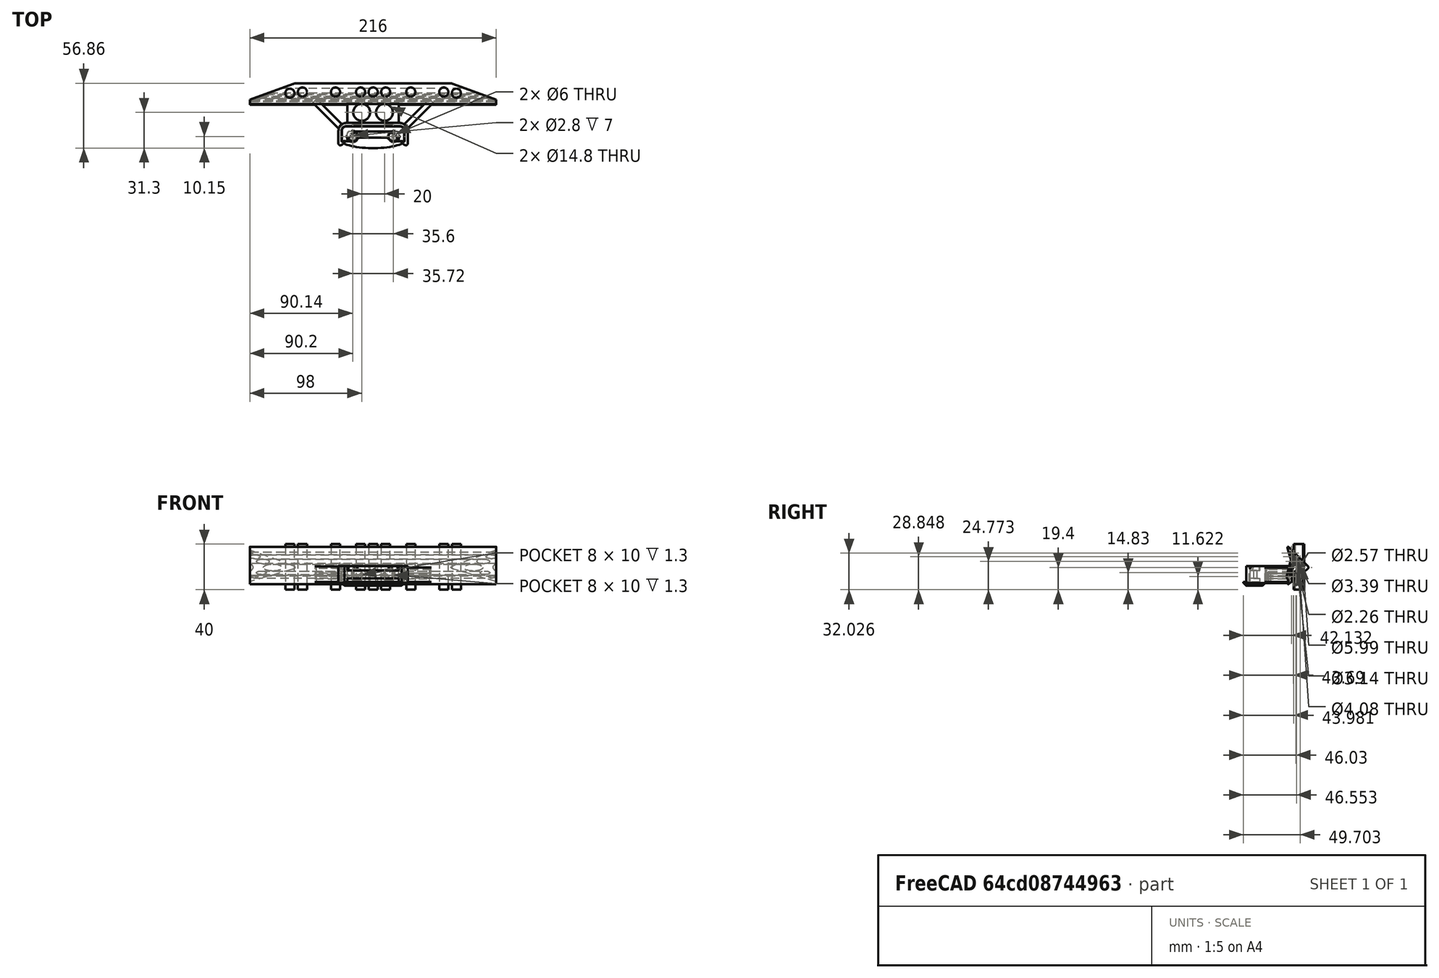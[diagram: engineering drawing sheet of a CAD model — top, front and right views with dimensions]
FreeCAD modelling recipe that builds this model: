
FCSTD DOCUMENT  (FreeCAD 0.21R0.20.1)
Label: 057
License: All rights reserved
LicenseURL: http://en.wikipedia.org/wiki/All_rights_reserved
objects: Part::Cylinder×29, Part::MultiFuse×13, Sketcher::SketchObject×7, Part::Extrusion×7, Part::Box×7, Part::Cut×6, Part::Fillet×5, Part::Chamfer×2
note: 76 computed .brp shape members not serialized (recipe doc carries the construction recipe); baked Part::Feature solids carry a one-line shape summary decoded from their .brp

FEATURE [Sketcher::SketchObject] Sketch  label="attatchmentPiece"
  FullyConstrained = true
  sketch-geometry (20):
    g0: LineSegment StartX=21.05 StartY=0 StartZ=0 EndX=21.05 EndY=-1 EndZ=0
    g1: LineSegment StartX=21.05 StartY=-1 StartZ=0 EndX=21.05 EndY=-4.3 EndZ=0
    g2: LineSegment StartX=-24.15 StartY=4.3 StartZ=0 EndX=21.05 EndY=4.3 EndZ=0
    g3: LineSegment StartX=21.05 StartY=0 StartZ=0 EndX=21.05 EndY=4.3 EndZ=0
    g4-g7: Circle x4 (B-spline internal-alignment scaffolding for g8; pole/knot coordinates omitted)
    g8: BSplineCurve PolesCount=4 KnotsCount=2 Degree=3 IsPeriodic=0
    g9: GeomPoint X=10.05 Y=-1 Z=0
    g10: GeomPoint X=14.55 Y=-4.3 Z=0
    g11: LineSegment StartX=10.05 StartY=-1 StartZ=0 EndX=-10.05 EndY=-1 EndZ=0
    g12: LineSegment StartX=14.55 StartY=-4.3 StartZ=0 EndX=21.05 EndY=-4.3 EndZ=0
    g13: LineSegment StartX=-24.15 StartY=4.3 StartZ=0 EndX=-24.15 EndY=-4.3 EndZ=0
    g14: LineSegment StartX=-13.15 StartY=-1 StartZ=0 EndX=-10.05 EndY=-1 EndZ=0
    g15: LineSegment StartX=-24.15 StartY=-4.3 StartZ=0 EndX=-19.35 EndY=-4.3 EndZ=0
    g16: LineSegment StartX=-19.35 StartY=-4.3 StartZ=0 EndX=-17.65 EndY=-4.3 EndZ=0
    g17: BSplineCurve PolesCount=4 KnotsCount=2 Degree=3 IsPeriodic=0
    g18: Circle CenterX=16.25 CenterY=0 CenterZ=0 NormalX=0 NormalY=0 NormalZ=1 AngleXU=0 Radius=1.4
    g19: Circle CenterX=-19.35 CenterY=0 CenterZ=0 NormalX=0 NormalY=0 NormalZ=1 AngleXU=0 Radius=1.4
  constraints (41):
    c: Vertical(g0)
    c: Coincident(g1,g0)
    c: Vertical(g1)
    c: Block(g0)
    c: Horizontal(g2)
    c: Vertical(g3)
    c: Coincident(g3,g2)
    c: Block(g2)
    c: Block(g3)
    c: Weight(g4) = 1
    c: Equal(g4,g5)
    c: Equal(g4,g6)
    c: Equal(g4,g7)
    c: InternalAlignment(g4-g7 -> g8) x4
    c: InternalAlignment(g9,g8)
    c: InternalAlignment(g10,g8)
    c: Block(g8)
    c: Coincident(g11,g8)
    c: Horizontal(g11)
    c: Coincident(g12,g8)
    c: Coincident(g12,g1)
    c: Horizontal(g12)
    c: Distance(g2) = 45.2
    c: Coincident(g13,g2)
    c: Vertical(g13)
    c: Horizontal(g14)
    c: Distance(g14) = 3.1
    c: Horizontal(g15)
    c: Block(g17)
    c: Coincident(g16,g15)
    c: Coincident(g16,g17)
    c: Horizontal(g16)
    c: Block(g16)
    c: Coincident(g17,g14)
    c: Block(g15)
    c: Block(g11)
    c: Block(g13)
    c: Distance(g15) = 4.8
    c: Distance(g16) = 1.7
    c: Block(g18)
    c: Block(g19)
FEATURE [Part::Extrusion] Extrude  label="attatchmentPiece001"
  Base = -> Sketch
  Dir = (0,0,1)
  DirMode = 2
  FaceMakerClass = Part::FaceMakerBullseye
  LengthFwd = 7
  LengthRev = 0
  Solid = true
  Symmetric = false
FEATURE [Sketcher::SketchObject] Sketch001  label="attatchmentPieceSurround"
  FullyConstrained = true
  sketch-geometry (18):
    g0: LineSegment StartX=25.85 StartY=-4.3 StartZ=0 EndX=21.05 EndY=-4.3 EndZ=0
    g1: LineSegment StartX=25.85 StartY=-4.3 StartZ=0 EndX=25.85 EndY=4.3 EndZ=0
    g2: LineSegment StartX=-21.05 StartY=8.9 StartZ=0 EndX=21.05 EndY=8.9 EndZ=0
    g3: Circle CenterX=21.05 CenterY=8.9 CenterZ=0 NormalX=0 NormalY=0 NormalZ=1 AngleXU=0 Radius=1
    g4: Circle CenterX=25.85 CenterY=8.9 CenterZ=0 NormalX=0 NormalY=0 NormalZ=1 AngleXU=0 Radius=1
    g5: Circle CenterX=25.85 CenterY=4.3 CenterZ=0 NormalX=0 NormalY=0 NormalZ=1 AngleXU=0 Radius=1
    g6: BSplineCurve PolesCount=3 KnotsCount=2 Degree=2 IsPeriodic=0
    g7: GeomPoint X=21.05 Y=8.9 Z=0
    g8: GeomPoint X=25.85 Y=4.3 Z=0
    g9: ArcOfCircle CenterX=19.45 CenterY=2.7 CenterZ=0 NormalX=0 NormalY=0 NormalZ=1 AngleXU=0 Radius=1.6 StartAngle=0 EndAngle=1.5708
    g10: LineSegment StartX=21.05 StartY=2.7 StartZ=0 EndX=21.05 EndY=-4.3 EndZ=0
    g11: BSplineCurve PolesCount=3 KnotsCount=2 Degree=2 IsPeriodic=0
    g12: LineSegment StartX=-28.95 StartY=-4.3 StartZ=0 EndX=-28.95 EndY=4.3 EndZ=0
    g13: LineSegment StartX=-24.15 StartY=-4.3 StartZ=0 EndX=-28.95 EndY=-4.3 EndZ=0
    g14: LineSegment StartX=-24.15 StartY=2.7 StartZ=0 EndX=-24.15 EndY=-4.3 EndZ=0
    g15: ArcOfCircle CenterX=-22.55 CenterY=2.7 CenterZ=0 NormalX=0 NormalY=0 NormalZ=1 AngleXU=0 Radius=1.6 StartAngle=1.5708 EndAngle=3.14159
    g16: LineSegment StartX=-24.15 StartY=8.9 StartZ=0 EndX=-21.05 EndY=8.9 EndZ=0
    g17: LineSegment StartX=-22.55 StartY=4.3 StartZ=0 EndX=19.45 EndY=4.3 EndZ=0
  constraints (38):
    c: Horizontal(g0)
    c: Vertical(g1)
    c: Coincident(g1,g0)
    c: Horizontal(g2)
    c: Distance(g2) = 42.1
    c: Block(g2)
    c: Coincident(g6,g2)
    c: Weight(g3) = 1
    c: Equal(g3,g4)
    c: Equal(g3,g5)
    c: Coincident(g6,g1)
    c: InternalAlignment(g3,g6)
    c: InternalAlignment(g4,g6)
    c: InternalAlignment(g5,g6)
    c: InternalAlignment(g7,g6)
    c: InternalAlignment(g8,g6)
    c: Block(g0)
    c: Block(g6)
    c: Block(g9)
    c: Coincident(g10,g9)
    c: Coincident(g10,g0)
    c: Vertical(g10)
    c: Horizontal(g13)
    c: Coincident(g12,g13)
    c: Vertical(g12)
    c: Coincident(g11,g12)
    c: Block(g12)
    c: Block(g11)
    c: Block(g15)
    c: Coincident(g14,g15)
    c: Coincident(g14,g13)
    c: Vertical(g14)
    c: Coincident(g16,g11)
    c: Coincident(g16,g2)
    c: Horizontal(g16)
    c: Coincident(g17,g15)
    c: Coincident(g17,g9)
    c: Horizontal(g17)
FEATURE [Part::Extrusion] Extrude001  label="attatchmentPieceSurround001"
  Base = -> Sketch001
  Dir = (0,0,1)
  DirMode = 2
  FaceMakerClass = Part::FaceMakerBullseye
  LengthFwd = 14.7
  LengthRev = 0
  Placement = pos=(0,0,-4.1) rot=(0,0,1;0rad)
  Solid = true
  Symmetric = false
FEATURE [Sketcher::SketchObject] Sketch002  label="attatchmentPieceEndScrewHoleCaps"
  FullyConstrained = true
  sketch-geometry (10):
    g0: ArcOfCircle CenterX=16.25 CenterY=0 CenterZ=0 NormalX=0 NormalY=0 NormalZ=1 AngleXU=0 Radius=4.3 StartAngle=2.05456 EndAngle=5.79942
    g1: LineSegment StartX=14.25 StartY=3.80657 StartZ=0 EndX=14.25 EndY=6 EndZ=0
    g2: LineSegment StartX=20.0566 StartY=-2 StartZ=0 EndX=22.25 EndY=-2 EndZ=0
    g3: LineSegment StartX=22.25 StartY=-2 StartZ=0 EndX=22.25 EndY=6 EndZ=0
    g4: LineSegment StartX=14.25 StartY=6 StartZ=0 EndX=22.25 EndY=6 EndZ=0
    g5: LineSegment StartX=-25.35 StartY=-2 StartZ=0 EndX=-25.35 EndY=6 EndZ=0
    g6: LineSegment StartX=-25.35 StartY=-2 StartZ=0 EndX=-23.1566 EndY=-2 EndZ=0
    g7: LineSegment StartX=-17.35 StartY=6 StartZ=0 EndX=-25.35 EndY=6 EndZ=0
    g8: LineSegment StartX=-17.35 StartY=3.80657 StartZ=0 EndX=-17.35 EndY=6 EndZ=0
    g9: ArcOfCircle CenterX=-19.35 CenterY=0 CenterZ=0 NormalX=0 NormalY=0 NormalZ=1 AngleXU=0 Radius=4.3 StartAngle=3.62536 EndAngle=7.37022
  constraints (25):
    c: Block(g0)
    c: Vertical(g1)
    c: Horizontal(g2)
    c: Coincident(g3,g2)
    c: Vertical(g3)
    c: Coincident(g4,g1)
    c: Horizontal(g4)
    c: Coincident(g3,g4)
    c: Block(g4)
    c: Block(g3)
    c: Coincident(g0,g1)
    c: Coincident(g0,g2)
    c: Block(g1)
    c: Block(g9)
    c: Horizontal(g6)
    c: Vertical(g8)
    c: Coincident(g7,g8)
    c: Horizontal(g7)
    c: Coincident(g5,g6)
    c: Vertical(g5)
    c: Coincident(g5,g7)
    c: Block(g7)
    c: Block(g5)
    c: Coincident(g9,g6)
    c: Coincident(g9,g8)
FEATURE [Part::Extrusion] Extrude002  label="attatchmentPieceEndScrewHoleCaps001"
  Base = -> Sketch002
  Dir = (0,0,1)
  DirMode = 2
  FaceMakerClass = Part::FaceMakerBullseye
  LengthFwd = 3.6
  LengthRev = 0
  Placement = pos=(0,0,7) rot=(0,0,1;0rad)
  Solid = true
  Symmetric = false
FEATURE [Sketcher::SketchObject] Sketch003  label="mainBumpperPieceAttatchment"
  FullyConstrained = true
  sketch-geometry (42):
    g0: Circle CenterX=28.85 CenterY=4.3 CenterZ=0 NormalX=0 NormalY=0 NormalZ=1 AngleXU=0 Radius=1
    g1: Circle CenterX=28.85 CenterY=11.9 CenterZ=0 NormalX=0 NormalY=0 NormalZ=1 AngleXU=0 Radius=1
    g2: Circle CenterX=21.05 CenterY=11.9 CenterZ=0 NormalX=0 NormalY=0 NormalZ=1 AngleXU=0 Radius=1
    g3: BSplineCurve PolesCount=3 KnotsCount=2 Degree=2 IsPeriodic=0
    g4: GeomPoint X=28.85 Y=4.3 Z=0
    g5: GeomPoint X=21.05 Y=11.9 Z=0
    g6: LineSegment StartX=-21.05 StartY=11.9 StartZ=0 EndX=21.05 EndY=11.9 EndZ=0
    g7: LineSegment StartX=28.85 StartY=4.3 StartZ=0 EndX=28.85 EndY=-4.3 EndZ=0
    g8: Circle CenterX=21.05 CenterY=9.2 CenterZ=0 NormalX=0 NormalY=0 NormalZ=1 AngleXU=0 Radius=1
    g9: Circle CenterX=26.15 CenterY=9.2 CenterZ=0 NormalX=0 NormalY=0 NormalZ=1 AngleXU=0 Radius=1
    g10: Circle CenterX=26.15 CenterY=4.3 CenterZ=0 NormalX=0 NormalY=0 NormalZ=1 AngleXU=0 Radius=1
    g11: BSplineCurve PolesCount=3 KnotsCount=2 Degree=2 IsPeriodic=0
    g12: GeomPoint X=21.05 Y=9.2 Z=0
    g13: GeomPoint X=26.15 Y=4.3 Z=0
    g14: LineSegment StartX=-21.05 StartY=9.2 StartZ=0 EndX=21.05 EndY=9.2 EndZ=0
    g15: LineSegment StartX=26.15 StartY=-4.3 StartZ=0 EndX=26.15 EndY=4.3 EndZ=0
    g16: LineSegment StartX=26.15 StartY=-4.3 StartZ=0 EndX=26.15 EndY=-4.6 EndZ=0
    g17: LineSegment StartX=23.45 StartY=-4.6 StartZ=0 EndX=26.15 EndY=-4.6 EndZ=0
    g18: LineSegment StartX=28.85 StartY=-4.3 StartZ=0 EndX=28.85 EndY=-7.9 EndZ=0
    g19: LineSegment StartX=23.45 StartY=-4.6 StartZ=0 EndX=23.45 EndY=-5.3 EndZ=0
    g20: Circle CenterX=28.85 CenterY=-7.9 CenterZ=0 NormalX=0 NormalY=0 NormalZ=1 AngleXU=0 Radius=1
    g21: Circle CenterX=26.15 CenterY=-8.2 CenterZ=0 NormalX=0 NormalY=0 NormalZ=1 AngleXU=0 Radius=1
    g22: Circle CenterX=23.45 CenterY=-5.3 CenterZ=0 NormalX=0 NormalY=0 NormalZ=1 AngleXU=0 Radius=1
    g23: BSplineCurve PolesCount=3 KnotsCount=2 Degree=2 IsPeriodic=0
    g24: GeomPoint X=28.85 Y=-7.9 Z=0
    g25: GeomPoint X=23.45 Y=-5.3 Z=0
    g26: LineSegment StartX=-21.05 StartY=9.2 StartZ=0 EndX=-24.15 EndY=9.2 EndZ=0
    g27: BSplineCurve PolesCount=3 KnotsCount=2 Degree=2 IsPeriodic=0
    g28: LineSegment StartX=-29.25 StartY=-4.3 StartZ=0 EndX=-29.25 EndY=-4.6 EndZ=0
    g29: LineSegment StartX=-29.25 StartY=-4.6 StartZ=0 EndX=-26.55 EndY=-4.6 EndZ=0
    g30: LineSegment StartX=-31.95 StartY=-4.3 StartZ=0 EndX=-31.95 EndY=-7.9 EndZ=0
    g31: LineSegment StartX=-26.55 StartY=-4.6 StartZ=0 EndX=-26.55 EndY=-5.3 EndZ=0
    g32: Circle CenterX=-31.95 CenterY=-7.9 CenterZ=0 NormalX=0 NormalY=0 NormalZ=1 AngleXU=0 Radius=1
    g33: Circle CenterX=-29.25 CenterY=-8.2 CenterZ=0 NormalX=0 NormalY=0 NormalZ=1 AngleXU=0 Radius=1
    g34: Circle CenterX=-26.55 CenterY=-5.3 CenterZ=0 NormalX=0 NormalY=0 NormalZ=1 AngleXU=0 Radius=1
    g35: BSplineCurve PolesCount=3 KnotsCount=2 Degree=2 IsPeriodic=0
    g36: GeomPoint X=-31.95 Y=-7.9 Z=0
    g37: GeomPoint X=-26.55 Y=-5.3 Z=0
    g38: LineSegment StartX=-31.95 StartY=4.3 StartZ=0 EndX=-31.95 EndY=-4.3 EndZ=0
    g39: LineSegment StartX=-29.25 StartY=-4.3 StartZ=0 EndX=-29.25 EndY=4.3 EndZ=0
    g40: BSplineCurve PolesCount=3 KnotsCount=2 Degree=2 IsPeriodic=0
    g41: LineSegment StartX=-21.05 StartY=11.9 StartZ=0 EndX=-24.15 EndY=11.9 EndZ=0
  constraints (78):
    c: Weight(g0) = 1
    c: Equal(g0,g1)
    c: Equal(g0,g2)
    c: InternalAlignment(g0,g3)
    c: InternalAlignment(g1,g3)
    c: InternalAlignment(g2,g3)
    c: InternalAlignment(g4,g3)
    c: InternalAlignment(g5,g3)
    c: Block(g3)
    c: Horizontal(g6)
    c: Vertical(g7)
    c: Block(g7)
    c: Block(g6)
    c: Weight(g8) = 1
    c: Equal(g8,g9)
    c: Equal(g8,g10)
    c: InternalAlignment(g8,g11)
    c: InternalAlignment(g9,g11)
    c: InternalAlignment(g10,g11)
    c: InternalAlignment(g12,g11)
    c: InternalAlignment(g13,g11)
    c: Horizontal(g14)
    c: Vertical(g15)
    c: Block(g11)
    c: Block(g15)
    c: Block(g14)
    c: Coincident(g16,g15)
    c: Vertical(g16)
    c: Distance(g16) = 0.3
    c: Horizontal(g17)
    c: Coincident(g17,g16)
    c: Coincident(g18,g7)
    c: Vertical(g18)
    c: Distance(g18) = 3.6
    c: Vertical(g19)
    c: Coincident(g19,g17)
    c: Coincident(g23,g18)
    c: Weight(g20) = 1
    c: Equal(g20,g21)
    c: Equal(g20,g22)
    c: Coincident(g23,g19)
    c: InternalAlignment(g20,g23)
    c: InternalAlignment(g21,g23)
    c: InternalAlignment(g22,g23)
    c: InternalAlignment(g24,g23)
    c: InternalAlignment(g25,g23)
    c: Block(g23)
    c: Horizontal(g26)
    c: Distance(g26) = 3.1
    c: Block(g27)
    c: Vertical(g38)
    c: Block(g38)
    c: Vertical(g39)
    c: Block(g40)
    c: Block(g39)
    c: Vertical(g28)
    c: Coincident(g28,g39)
    c: Coincident(g29,g28)
    c: Horizontal(g29)
    c: Vertical(g30)
    c: Coincident(g30,g38)
    c: Coincident(g31,g29)
    c: Vertical(g31)
    c: Coincident(g35,g30)
    c: Equal(g32,g33)
    c: Equal(g32,g34)
    c: Coincident(g35,g31)
    c: InternalAlignment(g32,g35)
    c: InternalAlignment(g33,g35)
    c: InternalAlignment(g34,g35)
    c: InternalAlignment(g36,g35)
    c: InternalAlignment(g37,g35)
    c: Block(g35)
    c: Coincident(g40,g26)
    c: Block(g29)
    c: Horizontal(g41)
    c: Equal(g26,g41) = 3.1
    c: Coincident(g41,g6)
FEATURE [Part::Box] Box  label="bumpperExtension"
  AttacherType = Attacher::AttachEngine3D
  Height = 14.7
  Length = 45.2
  Placement = pos=(-24.15,11.9,-4.1) rot=(0,0,1;0rad)
  Width = 18
FEATURE [Sketcher::SketchObject] Sketch004  label="bumpperMain"
  FullyConstrained = true
  Placement = pos=(0,0,0) rot=(0.57735,0.57735,0.57735;2.0944rad)
  sketch-geometry (62):
    g0: Circle CenterX=-3.12329 CenterY=2.49901 CenterZ=0 NormalX=0 NormalY=0 NormalZ=1 AngleXU=0 Radius=1
    g1: Circle CenterX=0 CenterY=0 CenterZ=0 NormalX=0 NormalY=0 NormalZ=1 AngleXU=0 Radius=1
    g2: Circle CenterX=-1.35243 CenterY=3.60648 CenterZ=0 NormalX=0 NormalY=0 NormalZ=1 AngleXU=0 Radius=1
    g3: BSplineCurve PolesCount=3 KnotsCount=2 Degree=2 IsPeriodic=0
    g4: GeomPoint X=-3.12329 Y=2.49901 Z=0
    g5: GeomPoint X=-1.35243 Y=3.60648 Z=0
    g6: Circle CenterX=-2.83953 CenterY=33.0261 CenterZ=0 NormalX=0 NormalY=0 NormalZ=1 AngleXU=0 Radius=1
    g7: Circle CenterX=0 CenterY=35.8434 CenterZ=0 NormalX=0 NormalY=0 NormalZ=1 AngleXU=0 Radius=1
    g8: Circle CenterX=-1.15771 CenterY=32.0146 CenterZ=0 NormalX=0 NormalY=0 NormalZ=1 AngleXU=0 Radius=1
    g9: BSplineCurve PolesCount=3 KnotsCount=2 Degree=2 IsPeriodic=0
    g10: GeomPoint X=-2.83953 Y=33.0261 Z=0
    g11: GeomPoint X=-1.15771 Y=32.0146 Z=0
    g12: Circle CenterX=-18.2963 CenterY=17.6904 CenterZ=0 NormalX=0 NormalY=0 NormalZ=1 AngleXU=0 Radius=1
    g13: Circle CenterX=-20 CenterY=16 CenterZ=0 NormalX=0 NormalY=0 NormalZ=1 AngleXU=0 Radius=1
    g14: Circle CenterX=-18.1259 CenterY=14.5008 CenterZ=0 NormalX=0 NormalY=0 NormalZ=1 AngleXU=0 Radius=1
    g15: BSplineCurve PolesCount=3 KnotsCount=2 Degree=2 IsPeriodic=0
    g16: GeomPoint X=-18.2963 Y=17.6904 Z=0
    g17: GeomPoint X=-18.1259 Y=14.5008 Z=0
    g18: LineSegment StartX=-18.2963 StartY=17.6904 StartZ=0 EndX=-2.83953 EndY=33.0261 EndZ=0
    g19: LineSegment StartX=-18.1259 StartY=14.5008 StartZ=0 EndX=-3.12329 EndY=2.49901 EndZ=0
    g20: Circle CenterX=-11.9527 CenterY=16 CenterZ=0 NormalX=0 NormalY=0 NormalZ=1 AngleXU=0 Radius=2.99582
    g21: Circle CenterX=-8.803 CenterY=21.3731 CenterZ=0 NormalX=0 NormalY=0 NormalZ=1 AngleXU=0 Radius=2.03939
    g22: Circle CenterX=-6.23123 CenterY=25.4475 CenterZ=0 NormalX=0 NormalY=0 NormalZ=1 AngleXU=0 Radius=1.69309
    g23: Circle CenterX=-4.38186 CenterY=28.6261 CenterZ=0 NormalX=0 NormalY=0 NormalZ=1 AngleXU=0 Radius=1.13029
    g24: Circle CenterX=-8.28033 CenterY=11.4296 CenterZ=0 NormalX=0 NormalY=0 NormalZ=1 AngleXU=0 Radius=1.57213
    g25: Circle CenterX=-5.93972 CenterY=8.22213 CenterZ=0 NormalX=0 NormalY=0 NormalZ=1 AngleXU=0 Radius=1.28743
    g26: Circle CenterX=-3.47023 CenterY=24.3665 CenterZ=0 NormalX=0 NormalY=0 NormalZ=1 AngleXU=0 Radius=1
    g27: Circle CenterX=-3.90437 CenterY=22.9307 CenterZ=0 NormalX=0 NormalY=0 NormalZ=1 AngleXU=0 Radius=1
    g28: Circle CenterX=-3.53772 CenterY=21.4762 CenterZ=0 NormalX=0 NormalY=0 NormalZ=1 AngleXU=0 Radius=1
    g29: BSplineCurve PolesCount=3 KnotsCount=2 Degree=2 IsPeriodic=0
    g30: GeomPoint X=-3.47023 Y=24.3665 Z=0
    g31: GeomPoint X=-3.53772 Y=21.4762 Z=0
    g32: LineSegment StartX=-1.15771 StartY=32.0146 StartZ=0 EndX=-3.47023 EndY=24.3665 EndZ=0
    g33: Circle CenterX=-5.41867 CenterY=17.9226 CenterZ=0 NormalX=0 NormalY=0 NormalZ=1 AngleXU=0 Radius=1
    g34: Circle CenterX=-6 CenterY=16 CenterZ=0 NormalX=0 NormalY=0 NormalZ=1 AngleXU=0 Radius=1
    g35: Circle CenterX=-5.22753 CenterY=13.9401 CenterZ=0 NormalX=0 NormalY=0 NormalZ=1 AngleXU=0 Radius=1
    g36: BSplineCurve PolesCount=3 KnotsCount=2 Degree=2 IsPeriodic=0
    g37: GeomPoint X=-5.41867 Y=17.9226 Z=0
    g38: GeomPoint X=-5.22753 Y=13.9401 Z=0
    g39: Circle CenterX=-3.98946 CenterY=10.6386 CenterZ=0 NormalX=0 NormalY=0 NormalZ=1 AngleXU=0 Radius=1
    g40: Circle CenterX=-2.58497 CenterY=6.89324 CenterZ=0 NormalX=0 NormalY=0 NormalZ=1 AngleXU=0 Radius=1
    g41: Circle CenterX=-3.11001 CenterY=10.8586 CenterZ=0 NormalX=0 NormalY=0 NormalZ=1 AngleXU=0 Radius=1
    g42: BSplineCurve PolesCount=3 KnotsCount=2 Degree=2 IsPeriodic=0
    g43: GeomPoint X=-3.98946 Y=10.6386 Z=0
    g44: GeomPoint X=-3.11001 Y=10.8586 Z=0
    g45: Circle CenterX=-1.35243 CenterY=3.60648 CenterZ=0 NormalX=0 NormalY=0 NormalZ=1 AngleXU=0 Radius=1
    g46: Circle CenterX=-1.76142 CenterY=4.69712 CenterZ=0 NormalX=0 NormalY=0 NormalZ=1 AngleXU=0 Radius=1
    g47: Circle CenterX=-1.05937 CenterY=5.79125 CenterZ=0 NormalX=0 NormalY=0 NormalZ=1 AngleXU=0 Radius=1
    g48: BSplineCurve PolesCount=3 KnotsCount=2 Degree=2 IsPeriodic=0
    g49: GeomPoint X=-1.35243 Y=3.60648 Z=0
    g50: GeomPoint X=-1.05937 Y=5.79125 Z=0
    g51: Circle CenterX=-0.519336 CenterY=6.6329 CenterZ=0 NormalX=0 NormalY=0 NormalZ=1 AngleXU=0 Radius=1
    g52: Circle CenterX=0 CenterY=7.44228 CenterZ=0 NormalX=0 NormalY=0 NormalZ=1 AngleXU=0 Radius=1
    g53: Circle CenterX=-0.244436 CenterY=8.41194 CenterZ=0 NormalX=0 NormalY=0 NormalZ=1 AngleXU=0 Radius=1
    g54: BSplineCurve PolesCount=3 KnotsCount=2 Degree=2 IsPeriodic=0
    g55: GeomPoint X=-0.519336 Y=6.6329 Z=0
    g56: GeomPoint X=-0.244436 Y=8.41194 Z=0
    g57: LineSegment StartX=-3.53772 StartY=21.4762 StartZ=0 EndX=-0.244436 EndY=8.41194 EndZ=0
    g58: LineSegment StartX=-5.22753 StartY=13.9401 StartZ=0 EndX=-3.98946 EndY=10.6386 EndZ=0
    g59: LineSegment StartX=-1.05937 StartY=5.79125 StartZ=0 EndX=-0.519336 EndY=6.6329 EndZ=0
    g60: BSplineCurve PolesCount=3 KnotsCount=2 Degree=2 IsPeriodic=0
    g61: LineSegment StartX=-4.0304 StartY=17.8099 StartZ=0 EndX=-3.11001 EndY=10.8586 EndZ=0
  constraints (96):
    c: Weight(g0) = 1
    c: Equal(g0,g1)
    c: Equal(g0,g2)
    c: InternalAlignment(g0,g3)
    c: InternalAlignment(g1,g3)
    c: InternalAlignment(g2,g3)
    c: InternalAlignment(g4,g3)
    c: InternalAlignment(g5,g3)
    c: Block(g3)
    c: Weight(g6) = 1
    c: Equal(g6,g7)
    c: Equal(g6,g8)
    c: InternalAlignment(g6,g9)
    c: InternalAlignment(g7,g9)
    c: InternalAlignment(g8,g9)
    c: InternalAlignment(g10,g9)
    c: InternalAlignment(g11,g9)
    c: Block(g9)
    c: Weight(g12) = 1
    c: Equal(g12,g13)
    c: Equal(g12,g14)
    c: InternalAlignment(g12,g15)
    c: InternalAlignment(g13,g15)
    c: InternalAlignment(g14,g15)
    c: InternalAlignment(g16,g15)
    c: InternalAlignment(g17,g15)
    c: Block(g15)
    c: Coincident(g18,g15)
    c: Coincident(g18,g9)
    c: Coincident(g19,g15)
    c: Coincident(g19,g3)
    c: Block(g25)
    c: Block(g24)
    c: Block(g20)
    c: Block(g21)
    c: Block(g22)
    c: Block(g23)
    c: Weight(g26) = 1
    c: Equal(g26,g27)
    c: Equal(g26,g28)
    c: InternalAlignment(g26,g29)
    c: InternalAlignment(g27,g29)
    c: InternalAlignment(g28,g29)
    c: InternalAlignment(g30,g29)
    c: InternalAlignment(g31,g29)
    c: Block(g29)
    c: Coincident(g32,g9)
    c: Coincident(g32,g29)
    c: Weight(g33) = 1
    c: Equal(g33,g34)
    c: Equal(g33,g35)
    c: InternalAlignment(g33,g36)
    c: InternalAlignment(g34,g36)
    c: InternalAlignment(g35,g36)
    c: InternalAlignment(g37,g36)
    c: InternalAlignment(g38,g36)
    c: Block(g36)
    c: Weight(g39) = 1
    c: Equal(g39,g40)
    c: Equal(g39,g41)
    c: InternalAlignment(g39,g42)
    c: InternalAlignment(g40,g42)
    c: InternalAlignment(g41,g42)
    c: InternalAlignment(g43,g42)
    c: InternalAlignment(g44,g42)
    c: Block(g42)
    c: Coincident(g48,g3)
    c: Weight(g45) = 1
    c: Equal(g45,g46)
    c: Equal(g45,g47)
    c: InternalAlignment(g45,g48)
    c: InternalAlignment(g46,g48)
    c: InternalAlignment(g47,g48)
    c: InternalAlignment(g49,g48)
    c: InternalAlignment(g50,g48)
    c: Block(g48)
    c: Weight(g51) = 1
    c: Equal(g51,g52)
    c: Equal(g51,g53)
    c: InternalAlignment(g51,g54)
    c: InternalAlignment(g52,g54)
    c: InternalAlignment(g53,g54)
    c: InternalAlignment(g55,g54)
    c: InternalAlignment(g56,g54)
    c: Block(g54)
    c: Coincident(g57,g29)
    c: Coincident(g57,g54)
    c: Block(g57)
    c: Coincident(g58,g36)
    c: Coincident(g58,g42)
    c: Coincident(g59,g48)
    c: Coincident(g59,g54)
    c: Block(g60)
    c: Coincident(g60,g36)
    c: Coincident(g61,g60)
    c: Coincident(g61,g42)
FEATURE [Part::Extrusion] Extrude004  label="bumpperMain001"
  Base = -> Sketch004
  Dir = (1,0,0)
  DirMode = 2
  FaceMakerClass = Part::FaceMakerBullseye
  LengthFwd = 216
  LengthRev = 0
  Placement = pos=(106.45,27.6,-6.6) rot=(0,0,1;3.14159rad)
  Solid = true
  Symmetric = false
FEATURE [Sketcher::SketchObject] Sketch005  label="attatchmentPieceBottom"
  FullyConstrained = true
  sketch-geometry (20):
    g0: LineSegment StartX=25.85 StartY=-4.3 StartZ=0 EndX=25.85 EndY=4.3 EndZ=0
    g1: LineSegment StartX=-21.05 StartY=8.9 StartZ=0 EndX=21.05 EndY=8.9 EndZ=0
    g2: Circle CenterX=21.05 CenterY=8.9 CenterZ=0 NormalX=0 NormalY=0 NormalZ=1 AngleXU=0 Radius=1
    g3: Circle CenterX=25.85 CenterY=8.9 CenterZ=0 NormalX=0 NormalY=0 NormalZ=1 AngleXU=0 Radius=1
    g4: Circle CenterX=25.85 CenterY=4.3 CenterZ=0 NormalX=0 NormalY=0 NormalZ=1 AngleXU=0 Radius=1
    g5: BSplineCurve PolesCount=3 KnotsCount=2 Degree=2 IsPeriodic=0
    g6: GeomPoint X=21.05 Y=8.9 Z=0
    g7: GeomPoint X=25.85 Y=4.3 Z=0
    g8: BSplineCurve PolesCount=3 KnotsCount=2 Degree=2 IsPeriodic=0
    g9: LineSegment StartX=-28.95 StartY=-4.3 StartZ=0 EndX=-28.95 EndY=4.3 EndZ=0
    g10: LineSegment StartX=-24.15 StartY=8.9 StartZ=0 EndX=-21.05 EndY=8.9 EndZ=0
    g11: Circle CenterX=-19.41 CenterY=0 CenterZ=0 NormalX=0 NormalY=0 NormalZ=1 AngleXU=0 Radius=3
    g12: Circle CenterX=16.3103 CenterY=0 CenterZ=0 NormalX=0 NormalY=0 NormalZ=1 AngleXU=0 Radius=3
    g13-g16: Circle x4 (B-spline internal-alignment scaffolding for g17; pole/knot coordinates omitted)
    g17: BSplineCurve PolesCount=4 KnotsCount=2 Degree=3 IsPeriodic=0
    g18: GeomPoint X=-28.95 Y=-4.3 Z=0
    g19: GeomPoint X=25.85 Y=-4.3 Z=0
  constraints (36):
    c: Vertical(g0)
    c: Horizontal(g1)
    c: Distance(g1) = 42.1
    c: Block(g1)
    c: Coincident(g5,g1)
    c: Weight(g2) = 1
    c: Equal(g2,g3)
    c: Equal(g2,g4)
    c: Coincident(g5,g0)
    c: InternalAlignment(g2,g5)
    c: InternalAlignment(g3,g5)
    c: InternalAlignment(g4,g5)
    c: InternalAlignment(g6,g5)
    c: InternalAlignment(g7,g5)
    c: Block(g5)
    c: Vertical(g9)
    c: Coincident(g8,g9)
    c: Block(g9)
    c: Block(g8)
    c: Coincident(g10,g8)
    c: Coincident(g10,g1)
    c: Horizontal(g10)
    c: PointOnObject(g12,g-1)
    c: PointOnObject(g11,g-1)
    c: Block(g11)
    c: Block(g12)
    c: Coincident(g17,g9)
    c: Weight(g13) = 1
    c: Equal(g13,g14)
    c: Equal(g13,g15)
    c: Equal(g13,g16)
    c: Coincident(g17,g0)
    c: InternalAlignment(g13-g16 -> g17) x4
    c: InternalAlignment(g18,g17)
    c: InternalAlignment(g19,g17)
    c: Block(g17)
FEATURE [Part::Extrusion] Extrude005  label="removeFromMainBumpperPieceAttatchment"
  Base = -> Sketch005
  Dir = (0,0,1)
  DirMode = 2
  FaceMakerClass = Part::FaceMakerBullseye
  LengthFwd = 3.2
  LengthRev = 0
  Placement = pos=(0,0,-6.2) rot=(0,0,1;0rad)
  Solid = true
  Symmetric = false
FEATURE [Part::Extrusion] Extrude006  label="mainBumpperPieceAttatchment001"
  Base = -> Sketch003
  Dir = (0,0,1)
  DirMode = 2
  FaceMakerClass = Part::FaceMakerBullseye
  LengthFwd = 14.7
  LengthRev = 0
  Placement = pos=(0,0,-4.1) rot=(0,0,1;0rad)
  Solid = true
  Symmetric = false
FEATURE [Part::Cylinder] Cylinder  label="removeFromBumpperExtension"
  Angle = 360
  AttacherType = Attacher::AttachEngine3D
  FirstAngle = 0
  Height = 20
  Placement = pos=(8.45,21.15,-8) rot=(0,0,1;0rad)
  Radius = 7.4
  SecondAngle = 0
FEATURE [Part::Cylinder] Cylinder001  label="removeFromBumpperExtension001"
  Angle = 360
  AttacherType = Attacher::AttachEngine3D
  FirstAngle = 0
  Height = 20
  Placement = pos=(-11.55,21.15,-8) rot=(0,0,1;0rad)
  Radius = 7.4
  SecondAngle = 0
FEATURE [Part::MultiFuse] Fusion  label="removeFromBumpperExtension002"
  Shapes = -> [Cylinder,Cylinder001]
FEATURE [Part::Cylinder] Cylinder002  label="removeFromBumpperExtension004"
  Angle = 360
  AttacherType = Attacher::AttachEngine3D
  FirstAngle = 0
  Height = 20
  Placement = pos=(8.45,21.15,-8) rot=(0,0,1;0rad)
  Radius = 7.4
  SecondAngle = 0
FEATURE [Part::Cylinder] Cylinder003  label="removeFromBumpperExtension005"
  Angle = 360
  AttacherType = Attacher::AttachEngine3D
  FirstAngle = 0
  Height = 20
  Placement = pos=(-11.55,21.15,-8) rot=(0,0,1;0rad)
  Radius = 7.4
  SecondAngle = 0
FEATURE [Part::MultiFuse] Fusion001  label="removeFromBumpperMain"
  Shapes = -> [Cylinder002,Cylinder003]
FEATURE [Part::Cut] Cut  label="bumpperExtension001"
  Base = -> Box
  Tool = -> Fusion
FEATURE [Part::Fillet] Fillet  label="bumpperExtension002"
  Base = -> Cut
  Edges = 4 edges r=3: [Edge2,Edge4,Edge9,Edge14]
FEATURE [Part::Box] Box001  label="bumpperExtensionBumpHole"
  AttacherType = Attacher::AttachEngine3D
  Height = 10
  Length = 8
  Placement = pos=(8.45,9.2,-1.8) rot=(0,0,1;0rad)
  Width = 1.3
FEATURE [Part::Box] Box002  label="bumpperExtensionBumpHole001"
  AttacherType = Attacher::AttachEngine3D
  Height = 10
  Length = 8
  Placement = pos=(-19.55,9.2,-1.8) rot=(0,0,1;0rad)
  Width = 1.3
FEATURE [Part::Box] Box003  label="attatchmentPieceSurroundBump"
  AttacherType = Attacher::AttachEngine3D
  Height = 9.2
  Length = 7.2
  Placement = pos=(8.85,8.9,-1.4) rot=(0,0,1;0rad)
  Width = 1.3
FEATURE [Part::Box] Box004  label="attatchmentPieceSurroundBump001"
  AttacherType = Attacher::AttachEngine3D
  Height = 9.2
  Length = 7.2
  Placement = pos=(-19.15,8.9,-1.4) rot=(0,0,1;0rad)
  Width = 1.3
FEATURE [Part::MultiFuse] Fusion002  label="attatchmentPieceSurroundBump002"
  Placement = pos=(0,-0.4,0) rot=(0,0,1;0rad)
  Shapes = -> [Box004,Box003]
FEATURE [Part::MultiFuse] Fusion003  label="bumpperExtensionBumpHole002"
  Shapes = -> [Box002,Box001]
FEATURE [Part::Cut] Cut002  label="mainBumpperPieceAttatchment002"
  Base = -> Extrude006
  Tool = -> Fusion003
FEATURE [Part::Fillet] Fillet003  label="attatchmentPieceEndScrewHoleCaps002"
  Base = -> Extrude002
  Edges = 6 edges r=2.4: [Edge4,Edge7,Edge15,Edge25,Edge28,Edge30]
FEATURE [Part::Fillet] Fillet004  label="attatchmentPieceSurround002"
  Base = -> Extrude001
  Edges = 3 edges r=1.2: [Edge19,Edge25,Edge31]
FEATURE [Part::Fillet] Fillet006  label="mainBumpperPieceAttatchment003"
  Base = -> Cut002
  Edges = 2 edges r=1.6: [Edge2,Edge55]
FEATURE [Sketcher::SketchObject] Sketch006  label="attatchmentPieceBottom002"
  FullyConstrained = true
  sketch-geometry (20):
    g0: LineSegment StartX=25.85 StartY=-4.3 StartZ=0 EndX=25.85 EndY=4.3 EndZ=0
    g1: LineSegment StartX=-21.05 StartY=8.9 StartZ=0 EndX=21.05 EndY=8.9 EndZ=0
    g2: Circle CenterX=21.05 CenterY=8.9 CenterZ=0 NormalX=0 NormalY=0 NormalZ=1 AngleXU=0 Radius=1
    g3: Circle CenterX=25.85 CenterY=8.9 CenterZ=0 NormalX=0 NormalY=0 NormalZ=1 AngleXU=0 Radius=1
    g4: Circle CenterX=25.85 CenterY=4.3 CenterZ=0 NormalX=0 NormalY=0 NormalZ=1 AngleXU=0 Radius=1
    g5: BSplineCurve PolesCount=3 KnotsCount=2 Degree=2 IsPeriodic=0
    g6: GeomPoint X=21.05 Y=8.9 Z=0
    g7: GeomPoint X=25.85 Y=4.3 Z=0
    g8: BSplineCurve PolesCount=3 KnotsCount=2 Degree=2 IsPeriodic=0
    g9: LineSegment StartX=-28.95 StartY=-4.3 StartZ=0 EndX=-28.95 EndY=4.3 EndZ=0
    g10: LineSegment StartX=-24.15 StartY=8.9 StartZ=0 EndX=-21.05 EndY=8.9 EndZ=0
    g11: Circle CenterX=-19.41 CenterY=0 CenterZ=0 NormalX=0 NormalY=0 NormalZ=1 AngleXU=0 Radius=3
    g12: Circle CenterX=16.3103 CenterY=0 CenterZ=0 NormalX=0 NormalY=0 NormalZ=1 AngleXU=0 Radius=3
    g13-g16: Circle x4 (B-spline internal-alignment scaffolding for g17; pole/knot coordinates omitted)
    g17: BSplineCurve PolesCount=4 KnotsCount=2 Degree=3 IsPeriodic=0
    g18: GeomPoint X=-28.95 Y=-4.3 Z=0
    g19: GeomPoint X=25.85 Y=-4.3 Z=0
  constraints (36):
    c: Vertical(g0)
    c: Horizontal(g1)
    c: Distance(g1) = 42.1
    c: Block(g1)
    c: Coincident(g5,g1)
    c: Weight(g2) = 1
    c: Equal(g2,g3)
    c: Equal(g2,g4)
    c: Coincident(g5,g0)
    c: InternalAlignment(g2,g5)
    c: InternalAlignment(g3,g5)
    c: InternalAlignment(g4,g5)
    c: InternalAlignment(g6,g5)
    c: InternalAlignment(g7,g5)
    c: Block(g5)
    c: Vertical(g9)
    c: Coincident(g8,g9)
    c: Block(g9)
    c: Block(g8)
    c: Coincident(g10,g8)
    c: Coincident(g10,g1)
    c: Horizontal(g10)
    c: PointOnObject(g12,g-1)
    c: PointOnObject(g11,g-1)
    c: Block(g11)
    c: Block(g12)
    c: Coincident(g17,g9)
    c: Weight(g13) = 1
    c: Equal(g13,g14)
    c: Equal(g13,g15)
    c: Equal(g13,g16)
    c: Coincident(g17,g0)
    c: InternalAlignment(g13-g16 -> g17) x4
    c: InternalAlignment(g18,g17)
    c: InternalAlignment(g19,g17)
    c: Block(g17)
FEATURE [Part::Extrusion] Extrude007  label="attatchmentPieceBottom003"
  Base = -> Sketch006
  Dir = (0,0,1)
  DirMode = 2
  FaceMakerClass = Part::FaceMakerBullseye
  LengthFwd = 3.2
  LengthRev = 0
  Placement = pos=(0,0,-6.5) rot=(0,0,1;0rad)
  Solid = true
  Symmetric = false
FEATURE [Part::Cut] Cut003  label="mainBumpperPieceAttatchment004"
  Base = -> Fillet006
  Tool = -> Extrude005
FEATURE [Part::Chamfer] Chamfer
  Base = -> Extrude007
  Edges = 2 edges r=2.4: [Edge23,Edge26]
FEATURE [Part::Chamfer] Chamfer001  label="attatchmentPieceBottom004"
  Base = -> Chamfer
  Edges = 7 edges r=2.4: [Edge14,Edge15,Edge16,Edge17,Edge18,Edge19,Edge20]
FEATURE [Part::Fillet] Fillet007  label="attatchmentPieceBottom005"
  Base = -> Chamfer001
  Edges = 7 edges r=1.2: [Edge1,Edge2,Edge3,Edge4,Edge5,Edge6,Edge7]
FEATURE [Part::MultiFuse] Fusion007  label="attatchment"
  Shapes = -> [Fillet007,Fillet004,Fillet003,Fusion002,Extrude]
FEATURE [Part::Cylinder] Cylinder004  label="brace"
  Angle = 360
  AttacherType = Attacher::AttachEngine3D
  FirstAngle = 0
  Height = 32
  Placement = pos=(-42,0,0) rot=(0,1,0;1.5708rad)
  Radius = 2.4
  SecondAngle = 0
FEATURE [Part::Cylinder] Cylinder005  label="brace001"
  Angle = 360
  AttacherType = Attacher::AttachEngine3D
  FirstAngle = 0
  Height = 10
  Placement = pos=(29,0,0) rot=(0,1,0;1.5708rad)
  Radius = 2
  SecondAngle = 0
FEATURE [Part::Cylinder] Cylinder006  label="brace002"
  Angle = 360
  AttacherType = Attacher::AttachEngine3D
  FirstAngle = 0
  Height = 10
  Placement = pos=(-42,0,0) rot=(0,1,0;1.5708rad)
  Radius = 2
  SecondAngle = 0
FEATURE [Part::MultiFuse] Fusion008  label="leftBrace"
  Placement = pos=(-23,1.4,8) rot=(0,0,1;-0.785398rad)
  Shapes = -> [Cylinder004,Cylinder006]
FEATURE [Part::Cylinder] Cylinder007  label="brace003"
  Angle = 360
  AttacherType = Attacher::AttachEngine3D
  FirstAngle = 0
  Height = 32
  Placement = pos=(29,0,0) rot=(0,1,0;1.5708rad)
  Radius = 2.4
  SecondAngle = 0
FEATURE [Part::MultiFuse] Fusion009  label="rightBrace"
  Placement = pos=(6.4,-12,7) rot=(0,0,1;0.785398rad)
  Shapes = -> [Cylinder007,Cylinder005]
FEATURE [Part::Box] Box005  label="removeFromMainRight"
  AttacherType = Attacher::AttachEngine3D
  Height = 40
  Length = 44
  Placement = pos=(66,47,-6) rot=(0,0,1;-0.349066rad)
  Width = 20
FEATURE [Part::Box] Box006  label="removeFromMainLeft"
  AttacherType = Attacher::AttachEngine3D
  Height = 40
  Length = 44
  Placement = pos=(-110.35,31.95,-6) rot=(0,0,1;0.349066rad)
  Width = 20
FEATURE [Part::Cylinder] Cylinder008  label="brace004"
  Angle = 360
  AttacherType = Attacher::AttachEngine3D
  FirstAngle = 0
  Height = 32
  Placement = pos=(-42,0,0) rot=(0,1,0;1.5708rad)
  Radius = 2.4
  SecondAngle = 0
FEATURE [Part::Cylinder] Cylinder009  label="brace005"
  Angle = 360
  AttacherType = Attacher::AttachEngine3D
  FirstAngle = 0
  Height = 10
  Placement = pos=(-42,0,0) rot=(0,1,0;1.5708rad)
  Radius = 2
  SecondAngle = 0
FEATURE [Part::MultiFuse] Fusion010  label="leftBrace001"
  Placement = pos=(-23,1.4,-1) rot=(0,0,-1;0.785398rad)
  Shapes = -> [Cylinder008,Cylinder009]
FEATURE [Part::Cylinder] Cylinder010  label="brace006"
  Angle = 360
  AttacherType = Attacher::AttachEngine3D
  FirstAngle = 0
  Height = 10
  Placement = pos=(29,0,0) rot=(0,1,0;1.5708rad)
  Radius = 2
  SecondAngle = 0
FEATURE [Part::Cylinder] Cylinder011  label="brace007"
  Angle = 360
  AttacherType = Attacher::AttachEngine3D
  FirstAngle = 0
  Height = 32
  Placement = pos=(29,0,0) rot=(0,1,0;1.5708rad)
  Radius = 2.4
  SecondAngle = 0
FEATURE [Part::MultiFuse] Fusion011  label="rightBrace001"
  Placement = pos=(6.4,-12,-1) rot=(0,0,1;0.785398rad)
  Shapes = -> [Cylinder011,Cylinder010]
FEATURE [Part::Cylinder] Cylinder012  label="brace008"
  Angle = 360
  AttacherType = Attacher::AttachEngine3D
  FirstAngle = 0
  Height = 32
  Placement = pos=(-42,0,0) rot=(0,1,0;1.5708rad)
  Radius = 2.4
  SecondAngle = 0
FEATURE [Part::Cylinder] Cylinder013  label="brace009"
  Angle = 360
  AttacherType = Attacher::AttachEngine3D
  FirstAngle = 0
  Height = 10
  Placement = pos=(-42,0,0) rot=(0,1,0;1.5708rad)
  Radius = 2
  SecondAngle = 0
FEATURE [Part::MultiFuse] Fusion012  label="leftBrace002"
  Placement = pos=(-23,1.4,6) rot=(0,0,-1;0.785398rad)
  Shapes = -> [Cylinder012,Cylinder013]
FEATURE [Part::Cylinder] Cylinder014  label="brace010"
  Angle = 360
  AttacherType = Attacher::AttachEngine3D
  FirstAngle = 0
  Height = 10
  Placement = pos=(29,0,0) rot=(0,1,0;1.5708rad)
  Radius = 2
  SecondAngle = 0
FEATURE [Part::Cylinder] Cylinder015  label="brace011"
  Angle = 360
  AttacherType = Attacher::AttachEngine3D
  FirstAngle = 0
  Height = 32
  Placement = pos=(29,0,0) rot=(0,1,0;1.5708rad)
  Radius = 2.4
  SecondAngle = 0
FEATURE [Part::MultiFuse] Fusion013  label="rightBrace002"
  Placement = pos=(6.4,-12,5) rot=(0,0,1;0.785398rad)
  Shapes = -> [Cylinder015,Cylinder014]
FEATURE [Part::Cylinder] Cylinder016  label="brace012"
  Angle = 360
  AttacherType = Attacher::AttachEngine3D
  FirstAngle = 0
  Height = 10
  Placement = pos=(29,0,0) rot=(0,1,0;1.5708rad)
  Radius = 2
  SecondAngle = 0
FEATURE [Part::Cylinder] Cylinder017  label="brace013"
  Angle = 360
  AttacherType = Attacher::AttachEngine3D
  FirstAngle = 0
  Height = 32
  Placement = pos=(29,0,0) rot=(0,1,0;1.5708rad)
  Radius = 2.4
  SecondAngle = 0
FEATURE [Part::MultiFuse] Fusion014  label="rightBrace003"
  Placement = pos=(6.4,-12,2) rot=(0,0,1;0.785398rad)
  Shapes = -> [Cylinder017,Cylinder016]
FEATURE [Part::Cylinder] Cylinder018  label="brace014"
  Angle = 360
  AttacherType = Attacher::AttachEngine3D
  FirstAngle = 0
  Height = 32
  Placement = pos=(-42,0,0) rot=(0,1,0;1.5708rad)
  Radius = 2.4
  SecondAngle = 0
FEATURE [Part::Cylinder] Cylinder019  label="brace015"
  Angle = 360
  AttacherType = Attacher::AttachEngine3D
  FirstAngle = 0
  Height = 10
  Placement = pos=(-42,0,0) rot=(0,1,0;1.5708rad)
  Radius = 2
  SecondAngle = 0
FEATURE [Part::MultiFuse] Fusion015  label="leftBrace003"
  Placement = pos=(-23,1.4,2) rot=(0,0,-1;0.785398rad)
  Shapes = -> [Cylinder018,Cylinder019]
FEATURE [Part::Cut] Cut004
  Base = -> Extrude004
  Tool = -> Fusion001
FEATURE [Part::Cut] Cut005
  Base = -> Cut004
  Tool = -> Box006
FEATURE [Part::Cut] Cut006  label="main"
  Base = -> Cut005
  Tool = -> Box005
FEATURE [Part::Cylinder] Cylinder020  label="removeFromMain"
  Angle = 360
  AttacherType = Attacher::AttachEngine3D
  FirstAngle = 0
  Height = 40
  Placement = pos=(-1.5,39,-10) rot=(0,0,1;0rad)
  Radius = 4
  SecondAngle = 0
FEATURE [Part::Cylinder] Cylinder021  label="removeFromMain001"
  Angle = 360
  AttacherType = Attacher::AttachEngine3D
  FirstAngle = 0
  Height = 40
  Placement = pos=(-12.5,39,-10) rot=(0,0,1;0rad)
  Radius = 4
  SecondAngle = 0
FEATURE [Part::Cylinder] Cylinder022  label="removeFromMain002"
  Angle = 360
  AttacherType = Attacher::AttachEngine3D
  FirstAngle = 0
  Height = 40
  Placement = pos=(9.5,39,-10) rot=(0,0,1;0rad)
  Radius = 4
  SecondAngle = 0
FEATURE [Part::Cylinder] Cylinder023  label="removeFromMain003"
  Angle = 360
  AttacherType = Attacher::AttachEngine3D
  FirstAngle = 0
  Height = 40
  Placement = pos=(-34.5,39,-10) rot=(0,0,1;0rad)
  Radius = 4
  SecondAngle = 0
FEATURE [Part::Cylinder] Cylinder024  label="removeFromMain004"
  Angle = 360
  AttacherType = Attacher::AttachEngine3D
  FirstAngle = 0
  Height = 40
  Placement = pos=(31.5,39,-10) rot=(0,0,1;0rad)
  Radius = 4
  SecondAngle = 0
FEATURE [Part::Cylinder] Cylinder025  label="removeFromMain005"
  Angle = 360
  AttacherType = Attacher::AttachEngine3D
  FirstAngle = 0
  Height = 40
  Placement = pos=(-63.5,39,-10) rot=(0,0,1;0rad)
  Radius = 4
  SecondAngle = 0
FEATURE [Part::Cylinder] Cylinder026  label="removeFromMain006"
  Angle = 360
  AttacherType = Attacher::AttachEngine3D
  FirstAngle = 0
  Height = 40
  Placement = pos=(60.5,39,-10) rot=(0,0,1;0rad)
  Radius = 4
  SecondAngle = 0
FEATURE [Part::Cylinder] Cylinder027  label="removeFromMain007"
  Angle = 360
  AttacherType = Attacher::AttachEngine3D
  FirstAngle = 0
  Height = 40
  Placement = pos=(-74.5,38,-10) rot=(0,0,1;0rad)
  Radius = 4
  SecondAngle = 0
FEATURE [Part::Cylinder] Cylinder028  label="removeFromMain008"
  Angle = 360
  AttacherType = Attacher::AttachEngine3D
  FirstAngle = 0
  Height = 40
  Placement = pos=(71.5,38,-10) rot=(0,0,1;0rad)
  Radius = 4
  SecondAngle = 0
